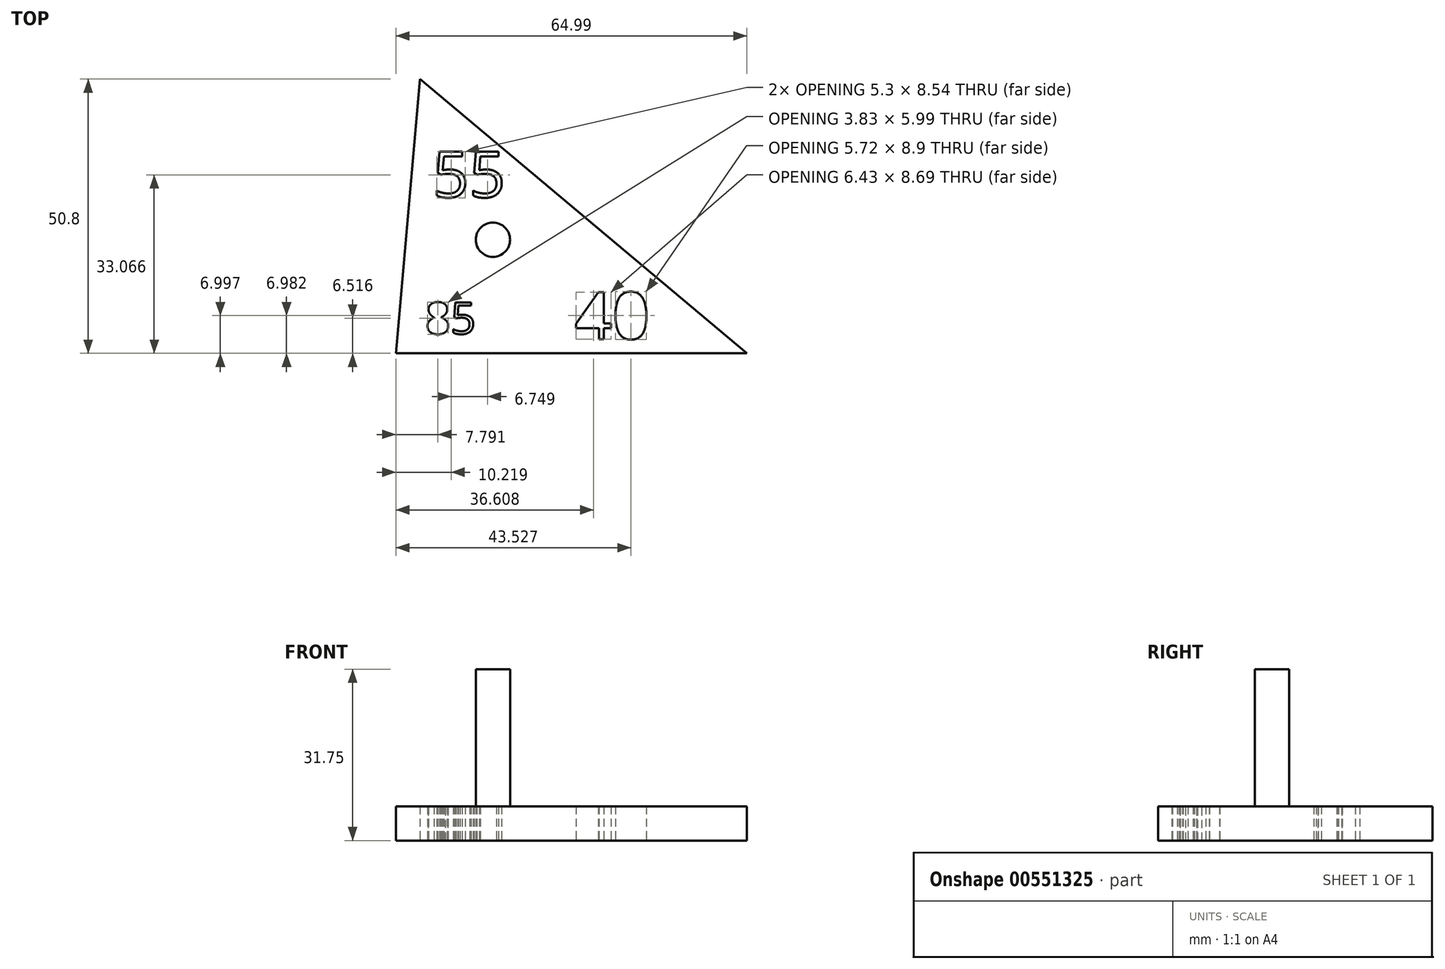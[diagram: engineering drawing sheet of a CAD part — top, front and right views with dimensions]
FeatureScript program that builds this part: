
annotation { "Feature Type Name" : "Feature", "Feature Type Description" : "" }
export const myFeature = defineFeature(function(context is Context, id is Id, definition is map)
    precondition{}
    {
        {
            var Q0;
            Q0=qCreatedBy(makeId("Top.planeOp"),FACE);
            var sketch = newSketch(context, id + "F0", { "sketchPlane" : qUnion([Q0])});
            skLineSegment(sketch, "E0", {"start": v(-60.54, 50.8) * mm, "end": v(-64.99, 0) * mm});
            skLineSegment(sketch, "E1", {"start": v(-64.99, 0) * mm, "end": v(0, 0) * mm});
            skLineSegment(sketch, "E2", {"start": v(0, 0) * mm, "end": v(-60.54, 50.8) * mm});
            skText(sketch, "E3", { "text": "85", "fontName": "OpenSans-Regular.ttf"});
            skText(sketch, "E4", { "text": "55", "fontName": "OpenSans-Regular.ttf"});
            skText(sketch, "E5", { "text": "40\n", "fontName": "OpenSans-Regular.ttf"});
            const initialGuessF0  = {"E3": [-0.05953, 0.0036, 1, 0, 0.00588], "E4": [-0.05819, 0.02891, 1, 0, 0.0085], "E5": [-0.03185, 0.00265, 1, 0, 0.00872]};
            skSetInitialGuess(sketch, initialGuessF0);
            skSolve(sketch);
        }
        {
            var Q0;
            Q0=makeQuery(id+"F0.imprint","IMPRINT",FACE,{"disambiguationData":[TD([[makeQuery(id+"F0.imprint","IMPRINT",EDGE,{"derivedFrom":sQuery(id+"F0.wireOp",EDGE,"E0")}),1.0]])]});
            extrude(context, id + "F1", {"entities" : qUnion([Q0]), "depth" : 6.35 * mm, "offsetDistance" : 25.4 * mm});
        }
        {
            var Q0;
            Q0=makeQuery(id+"F1.opExtrude","CAP_FACE",FACE,{"disambiguationData":[OSD([sQuery(id+"F0.wireOp",EDGE,"E0"),sQuery(id+"F0.wireOp",EDGE,"E1"),sQuery(id+"F0.wireOp",EDGE,"E2"),sQuery(id+"F0.wireOp",EDGE,"E3.sketch_text.stroke-0"),sQuery(id+"F0.wireOp",EDGE,"E3.sketch_text.stroke-1"),sQuery(id+"F0.wireOp",EDGE,"E3.sketch_text.stroke-2"),sQuery(id+"F0.wireOp",EDGE,"E3.sketch_text.stroke-3"),sQuery(id+"F0.wireOp",EDGE,"E3.sketch_text.stroke-4"),sQuery(id+"F0.wireOp",EDGE,"E3.sketch_text.stroke-5"),sQuery(id+"F0.wireOp",EDGE,"E3.sketch_text.stroke-6"),sQuery(id+"F0.wireOp",EDGE,"E3.sketch_text.stroke-7"),sQuery(id+"F0.wireOp",EDGE,"E3.sketch_text.stroke-8"),sQuery(id+"F0.wireOp",EDGE,"E3.sketch_text.stroke-9"),sQuery(id+"F0.wireOp",EDGE,"E3.sketch_text.stroke-10"),sQuery(id+"F0.wireOp",EDGE,"E3.sketch_text.stroke-11"),sQuery(id+"F0.wireOp",EDGE,"E3.sketch_text.stroke-12"),sQuery(id+"F0.wireOp",EDGE,"E3.sketch_text.stroke-13"),sQuery(id+"F0.wireOp",EDGE,"E3.sketch_text.stroke-14"),sQuery(id+"F0.wireOp",EDGE,"E3.sketch_text.stroke-31"),sQuery(id+"F0.wireOp",EDGE,"E3.sketch_text.stroke-32"),sQuery(id+"F0.wireOp",EDGE,"E3.sketch_text.stroke-33"),sQuery(id+"F0.wireOp",EDGE,"E3.sketch_text.stroke-34"),sQuery(id+"F0.wireOp",EDGE,"E3.sketch_text.stroke-35"),sQuery(id+"F0.wireOp",EDGE,"E3.sketch_text.stroke-36"),sQuery(id+"F0.wireOp",EDGE,"E3.sketch_text.stroke-37"),sQuery(id+"F0.wireOp",EDGE,"E3.sketch_text.stroke-38"),sQuery(id+"F0.wireOp",EDGE,"E3.sketch_text.stroke-39"),sQuery(id+"F0.wireOp",EDGE,"E3.sketch_text.stroke-40"),sQuery(id+"F0.wireOp",EDGE,"E3.sketch_text.stroke-41"),sQuery(id+"F0.wireOp",EDGE,"E3.sketch_text.stroke-42"),sQuery(id+"F0.wireOp",EDGE,"E3.sketch_text.stroke-43"),sQuery(id+"F0.wireOp",EDGE,"E3.sketch_text.stroke-44"),sQuery(id+"F0.wireOp",EDGE,"E3.sketch_text.stroke-45"),sQuery(id+"F0.wireOp",EDGE,"E3.sketch_text.stroke-46"),sQuery(id+"F0.wireOp",EDGE,"E3.sketch_text.stroke-47"),sQuery(id+"F0.wireOp",EDGE,"E3.sketch_text.stroke-48"),sQuery(id+"F0.wireOp",EDGE,"E3.sketch_text.stroke-49"),sQuery(id+"F0.wireOp",EDGE,"E4.sketch_text.stroke-0"),sQuery(id+"F0.wireOp",EDGE,"E4.sketch_text.stroke-1"),sQuery(id+"F0.wireOp",EDGE,"E4.sketch_text.stroke-2"),sQuery(id+"F0.wireOp",EDGE,"E4.sketch_text.stroke-3"),sQuery(id+"F0.wireOp",EDGE,"E4.sketch_text.stroke-4"),sQuery(id+"F0.wireOp",EDGE,"E4.sketch_text.stroke-5"),sQuery(id+"F0.wireOp",EDGE,"E4.sketch_text.stroke-6"),sQuery(id+"F0.wireOp",EDGE,"E4.sketch_text.stroke-7"),sQuery(id+"F0.wireOp",EDGE,"E4.sketch_text.stroke-8"),sQuery(id+"F0.wireOp",EDGE,"E4.sketch_text.stroke-9"),sQuery(id+"F0.wireOp",EDGE,"E4.sketch_text.stroke-10"),sQuery(id+"F0.wireOp",EDGE,"E4.sketch_text.stroke-11"),sQuery(id+"F0.wireOp",EDGE,"E4.sketch_text.stroke-12"),sQuery(id+"F0.wireOp",EDGE,"E4.sketch_text.stroke-13"),sQuery(id+"F0.wireOp",EDGE,"E4.sketch_text.stroke-14"),sQuery(id+"F0.wireOp",EDGE,"E4.sketch_text.stroke-15"),sQuery(id+"F0.wireOp",EDGE,"E4.sketch_text.stroke-16"),sQuery(id+"F0.wireOp",EDGE,"E4.sketch_text.stroke-17"),sQuery(id+"F0.wireOp",EDGE,"E4.sketch_text.stroke-18"),sQuery(id+"F0.wireOp",EDGE,"E4.sketch_text.stroke-19"),sQuery(id+"F0.wireOp",EDGE,"E4.sketch_text.stroke-20"),sQuery(id+"F0.wireOp",EDGE,"E4.sketch_text.stroke-21"),sQuery(id+"F0.wireOp",EDGE,"E4.sketch_text.stroke-22"),sQuery(id+"F0.wireOp",EDGE,"E4.sketch_text.stroke-23"),sQuery(id+"F0.wireOp",EDGE,"E4.sketch_text.stroke-24"),sQuery(id+"F0.wireOp",EDGE,"E4.sketch_text.stroke-25"),sQuery(id+"F0.wireOp",EDGE,"E4.sketch_text.stroke-26"),sQuery(id+"F0.wireOp",EDGE,"E4.sketch_text.stroke-27"),sQuery(id+"F0.wireOp",EDGE,"E4.sketch_text.stroke-28"),sQuery(id+"F0.wireOp",EDGE,"E4.sketch_text.stroke-29"),sQuery(id+"F0.wireOp",EDGE,"E4.sketch_text.stroke-30"),sQuery(id+"F0.wireOp",EDGE,"E4.sketch_text.stroke-31"),sQuery(id+"F0.wireOp",EDGE,"E4.sketch_text.stroke-32"),sQuery(id+"F0.wireOp",EDGE,"E4.sketch_text.stroke-33"),sQuery(id+"F0.wireOp",EDGE,"E4.sketch_text.stroke-34"),sQuery(id+"F0.wireOp",EDGE,"E4.sketch_text.stroke-35"),sQuery(id+"F0.wireOp",EDGE,"E4.sketch_text.stroke-36"),sQuery(id+"F0.wireOp",EDGE,"E4.sketch_text.stroke-37"),sQuery(id+"F0.wireOp",EDGE,"E5.sketch_text.stroke-0"),sQuery(id+"F0.wireOp",EDGE,"E5.sketch_text.stroke-1"),sQuery(id+"F0.wireOp",EDGE,"E5.sketch_text.stroke-2"),sQuery(id+"F0.wireOp",EDGE,"E5.sketch_text.stroke-3"),sQuery(id+"F0.wireOp",EDGE,"E5.sketch_text.stroke-4"),sQuery(id+"F0.wireOp",EDGE,"E5.sketch_text.stroke-5"),sQuery(id+"F0.wireOp",EDGE,"E5.sketch_text.stroke-6"),sQuery(id+"F0.wireOp",EDGE,"E5.sketch_text.stroke-7"),sQuery(id+"F0.wireOp",EDGE,"E5.sketch_text.stroke-8"),sQuery(id+"F0.wireOp",EDGE,"E5.sketch_text.stroke-9"),sQuery(id+"F0.wireOp",EDGE,"E5.sketch_text.stroke-10"),sQuery(id+"F0.wireOp",EDGE,"E5.sketch_text.stroke-17"),sQuery(id+"F0.wireOp",EDGE,"E5.sketch_text.stroke-18"),sQuery(id+"F0.wireOp",EDGE,"E5.sketch_text.stroke-19"),sQuery(id+"F0.wireOp",EDGE,"E5.sketch_text.stroke-20"),sQuery(id+"F0.wireOp",EDGE,"E5.sketch_text.stroke-21"),sQuery(id+"F0.wireOp",EDGE,"E5.sketch_text.stroke-22"),sQuery(id+"F0.wireOp",EDGE,"E5.sketch_text.stroke-23"),sQuery(id+"F0.wireOp",EDGE,"E5.sketch_text.stroke-24")])],"isStart":false});
            var sketch = newSketch(context, id + "F2", { "sketchPlane" : qUnion([Q0])});
            skCircle(sketch, "E6", {"center": v(-47.02, 21.05) * mm, "radius": 3.18 * mm});
            skSolve(sketch);
        }
        {
            var Q0;
            Q0=makeQuery(id+"F2.imprint","IMPRINT",FACE,{"disambiguationData":[TD([[makeQuery(id+"F2.imprint","IMPRINT",EDGE,{"derivedFrom":sQuery(id+"F2.wireOp",EDGE,"E6")}),1.0]])]});
            extrude(context, id + "F3", {"entities" : qUnion([Q0]), "operationType" : NewBodyOperationType.ADD, "depth" : 25.4 * mm, "offsetDistance" : 25.4 * mm});
        }
    });
